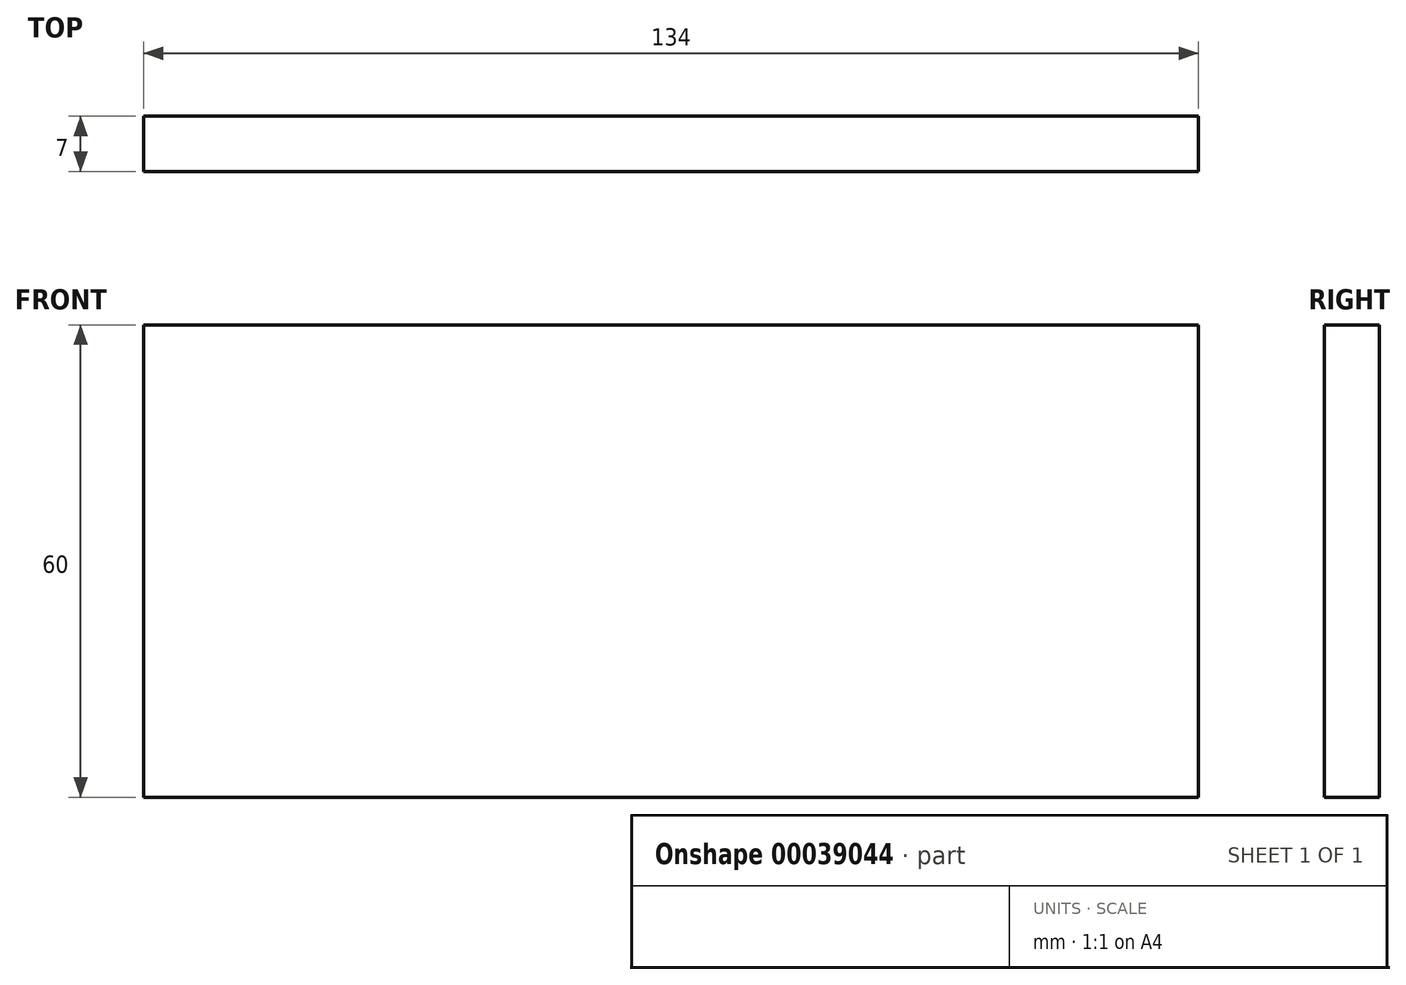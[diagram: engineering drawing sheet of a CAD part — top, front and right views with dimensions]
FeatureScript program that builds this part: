
annotation { "Feature Type Name" : "Feature", "Feature Type Description" : "" }
export const myFeature = defineFeature(function(context is Context, id is Id, definition is map)
    precondition{}
    {
        {
            var Q0;
            Q0=qCreatedBy(makeId("Right.planeOp"),FACE);
            var sketch = newSketch(context, id + "F0", { "sketchPlane" : qUnion([Q0])});
            skLineSegment(sketch, "E0.0", {"start": v(-3.25, 35.83) * mm, "end": v(-3.25, 0.83) * mm});
            skLineSegment(sketch, "E1.0", {"start": v(3.75, 35.83) * mm, "end": v(3.75, -24.17) * mm});
            skLineSegment(sketch, "E2.0", {"start": v(3.75, 35.83) * mm, "end": v(-3.25, 35.83) * mm});
            skLineSegment(sketch, "E3.0", {"start": v(-3.25, -24.17) * mm, "end": v(3.75, -24.17) * mm});
            skLineSegment(sketch, "E4", {"start": v(-3.25, 0.83) * mm, "end": v(-3.25, -24.17) * mm});
            skPoint(sketch, "E5.orphan", {"position": v(-10.25, -24.17) * mm});
            skSolve(sketch);
        }
        {
            var Q0;
            Q0 = qSketchRegion(id + "F0", true);
            extrude(context, id + "F1", {"entities" : qUnion([Q0]), "depth" : (150 - 16) * mm});
        }
    });
